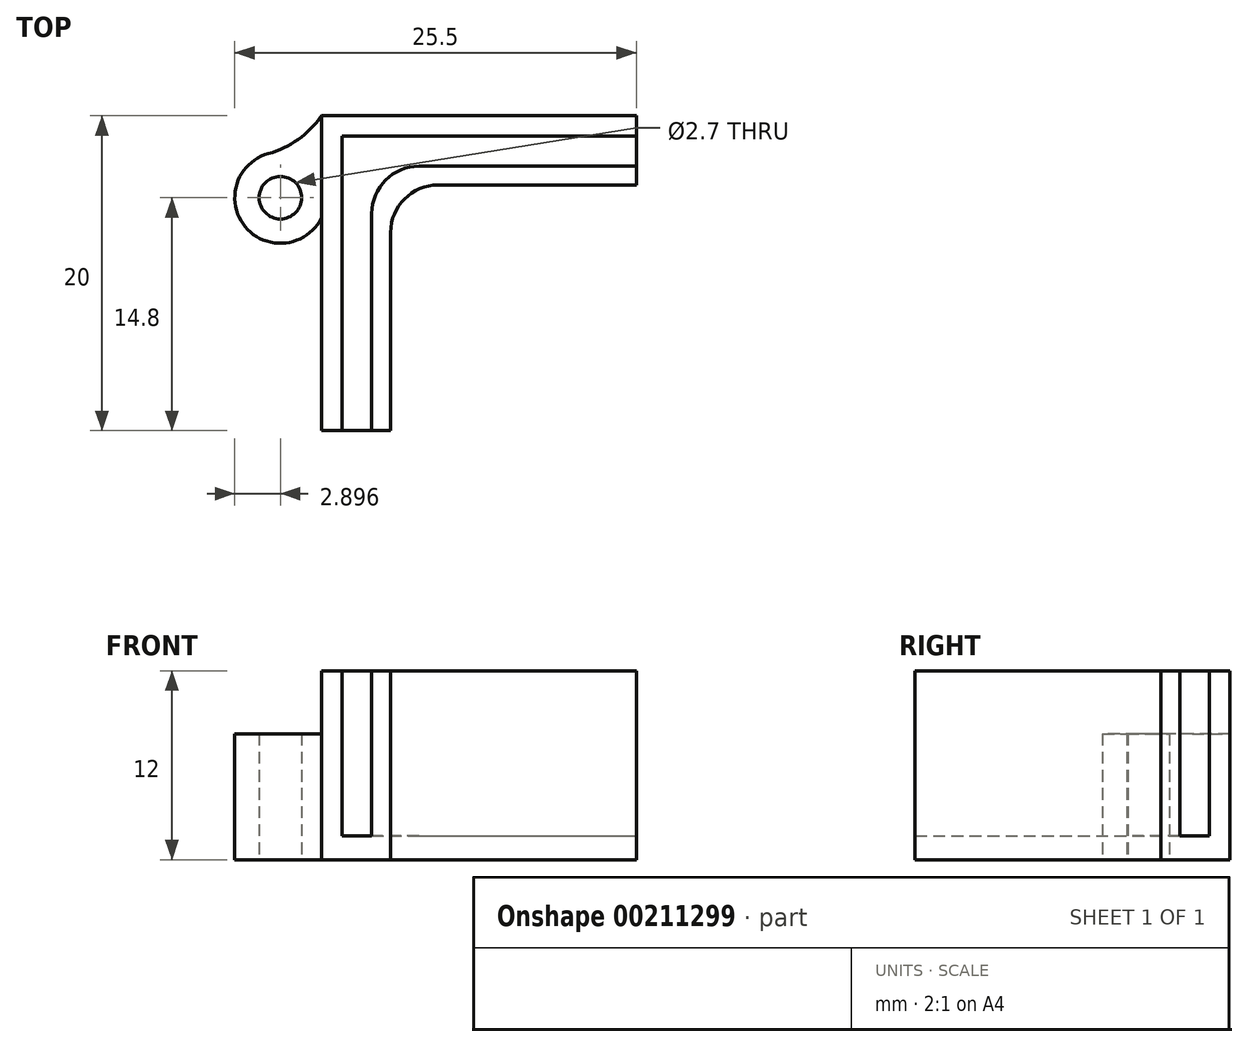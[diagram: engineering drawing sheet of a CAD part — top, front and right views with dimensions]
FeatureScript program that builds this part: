
annotation { "Feature Type Name" : "Feature", "Feature Type Description" : "" }
export const myFeature = defineFeature(function(context is Context, id is Id, definition is map)
    precondition{}
    {
        {
            var Q0;
            Q0=qCreatedBy(makeId("Top.planeOp"),FACE);
            var sketch = newSketch(context, id + "F0", { "sketchPlane" : qUnion([Q0])});
            skLineSegment(sketch, "E0", {"start": v(-7.96, 0) * mm, "end": v(-7.96, 20) * mm});
            skLineSegment(sketch, "E1", {"start": v(-7.96, 20) * mm, "end": v(12.04, 20) * mm});
            skLineSegment(sketch, "E2", {"start": v(12.04, 20) * mm, "end": v(12.04, 15.6) * mm});
            skLineSegment(sketch, "E3", {"start": v(12.04, 15.6) * mm, "end": v(-3.56, 15.6) * mm});
            skLineSegment(sketch, "E4", {"start": v(-3.56, 15.6) * mm, "end": v(-3.56, 0) * mm});
            skLineSegment(sketch, "E5", {"start": v(-3.56, 0) * mm, "end": v(-7.96, 0) * mm});
            skSolve(sketch);
        }
        {
            var Q0;
            Q0=makeQuery(id+"F0.imprint","IMPRINT",FACE,{"disambiguationData":[TD([[makeQuery(id+"F0.imprint","IMPRINT",EDGE,{"derivedFrom":sQuery(id+"F0.wireOp",EDGE,"E0")}),-1.0]])]});
            extrude(context, id + "F1", {"entities" : qUnion([Q0]), "depth" : 12 * mm});
        }
        {
            var Q0;
            Q0=makeQuery(id+"F1.opExtrude","CAP_FACE",FACE,{"disambiguationData":[OSD([sQuery(id+"F0.wireOp",EDGE,"E0"),sQuery(id+"F0.wireOp",EDGE,"E1"),sQuery(id+"F0.wireOp",EDGE,"E2"),sQuery(id+"F0.wireOp",EDGE,"E3"),sQuery(id+"F0.wireOp",EDGE,"E4"),sQuery(id+"F0.wireOp",EDGE,"E5")])],"isStart":false});
            var sketch = newSketch(context, id + "F2", { "sketchPlane" : qUnion([Q0])});
            skLineSegment(sketch, "E6", {"start": v(-5.76, 0) * mm, "end": v(-5.76, 17.8) * mm});
            skPoint(sketch, "E6.endSnap0", {"position": v(12.04, 17.8) * mm});
            skLineSegment(sketch, "E7", {"start": v(-5.76, 17.8) * mm, "end": v(12.04, 17.8) * mm});
            skLineSegment(sketch, "E8.0", {"start": v(-4.76, 16.8) * mm, "end": v(12.04, 16.8) * mm});
            skLineSegment(sketch, "E8.1", {"start": v(-4.76, 0) * mm, "end": v(-4.76, 16.8) * mm});
            skLineSegment(sketch, "E9.0", {"start": v(-6.66, 18.7) * mm, "end": v(12.04, 18.7) * mm});
            skLineSegment(sketch, "E9.1", {"start": v(-6.66, 0) * mm, "end": v(-6.66, 18.7) * mm});
            skSolve(sketch);
        }
        {
            var Q0;
            {var subQ2=sQuery(id+"F2.wireOp",EDGE,"E6");Q0=makeQuery(id+"F2.imprint","IMPRINT",FACE,{"disambiguationData":[TD([[makeQuery(id+"F2.imprint","IMPRINT",EDGE,{"derivedFrom":subQ2}),1.0]])]});}
            var Q1;
            {var subQ2=sQuery(id+"F2.wireOp",EDGE,"E6");Q1=makeQuery(id+"F2.imprint","IMPRINT",FACE,{"disambiguationData":[TD([[makeQuery(id+"F2.imprint","IMPRINT",EDGE,{"derivedFrom":subQ2}),-1.0]])]});}
            extrude(context, id + "F3", {"entities" : qUnion([Q0, Q1]), "operationType" : NewBodyOperationType.REMOVE, "oppositeDirection" : true, "depth" : 10.5 * mm});
        }
        {
            var Q0;
            Q0=makeQuery(id+"F3.boolean.opBoolean","COPY",EDGE,{"derivedFrom":makeQuery(id+"F3.opExtrude","SWEPT_EDGE",EDGE,{"disambiguationData":[OSD([sQuery(id+"F2.wireOp",EDGE,"E8.0"),sQuery(id+"F2.wireOp",EDGE,"E8.1")])]})});
            var Q1;
            Q1=makeQuery(id+"F1.opExtrude","SWEPT_EDGE",EDGE,{"disambiguationData":[OSD([sQuery(id+"F0.wireOp",EDGE,"E3"),sQuery(id+"F0.wireOp",EDGE,"E4")])]});
            fillet(context, id + "F4", {"entities" : qUnion([Q0, Q1]), "radius" : 3 * mm, "tangentPropagation" : true, "allowEdgeOverflow" : false});
        }
        {
            var Q0;
            Q0=qCreatedBy(makeId("Top.planeOp"),FACE);
            var sketch = newSketch(context, id + "F5", { "sketchPlane" : qUnion([Q0])});
            skCircle(sketch, "E10", {"center": v(-10.56, 14.8) * mm, "radius": 2.9 * mm});
            skCircle(sketch, "E11", {"center": v(-10.56, 14.8) * mm, "radius": 1.35 * mm});
            skArc(sketch, "E12", {"start": v(-11.33, 17.6) * mm, "mid": v(-9.43, 18.5) * mm, "end": v(-7.96, 20) * mm});
            skLineSegment(sketch, "E13", {"start": v(-10.56, 14.8) * mm, "end": v(17.51, 14.8) * mm, "construction": true});
            skArc(sketch, "E14.MirrorCS", {"start": v(-11.33, 12) * mm, "mid": v(-9.43, 11.1) * mm, "end": v(-7.96, 9.6) * mm});
            skLineSegment(sketch, "E15", {"start": v(-7.96, 20) * mm, "end": v(-7.96, 9.6) * mm});
            skSolve(sketch);
        }
        {
            var Q0;
            {var subQ0=sQuery(id+"F5.wireOp",EDGE,"E12");Q0=makeQuery(id+"F5.imprint","IMPRINT",FACE,{"disambiguationData":[TD([[makeQuery(id+"F5.imprint","IMPRINT",EDGE,{"derivedFrom":subQ0}),-1.0]])]});}
            var Q1;
            {var subQ0=sQuery(id+"F5.wireOp",EDGE,"E14.MirrorCS");Q1=makeQuery(id+"F5.imprint","IMPRINT",FACE,{"disambiguationData":[TD([[makeQuery(id+"F5.imprint","IMPRINT",EDGE,{"derivedFrom":subQ0}),1.0]])]});}
            var Q2;
            Q2=makeQuery(id+"F5.imprint","IMPRINT",FACE,{"disambiguationData":[TD([[makeQuery(id+"F5.imprint","IMPRINT",EDGE,{"derivedFrom":sQuery(id+"F5.wireOp",EDGE,"E11")}),-1.0]])]});
            extrude(context, id + "F6", {"entities" : qUnion([Q0, Q1, Q2]), "operationType" : NewBodyOperationType.ADD, "depth" : 8 * mm});
        }
    });
